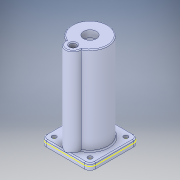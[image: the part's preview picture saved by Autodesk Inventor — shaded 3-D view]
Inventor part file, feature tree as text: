
AUTODESK INVENTOR PART (.ipt)
format: ipt  version: 2018 (Build 220112000, 112)  size: 350,208 bytes
history: native  units: in
note: dims shown in document units (in); Inventor stores cm internally (conversion verified against a paired STEP export)
features: extrude x16, sketch x13, projected_geometry x13, fillet x6, chamfer x1, revolve x1, other x1
ambient origin geometry x8: Origin, YZ Plane, XZ Plane, XY Plane, X Axis, Y Axis, Z Axis, Center Point
bodies: Solid1 (feature_tree)
feature tree (51):
  extrude  "Extrusion1"  TaperAngle=0.0deg  [1 undecoded]
  sketch  "Sketch2"  dims[d4=0.3937in d5=0.0in d6=1.0in d7=0.0in]
  extrude  "Extrusion2"  Depth=1.0in TaperAngle=0.0deg
  extrude  "Extrusion3"  Depth=0.9252in
  sketch  "Sketch3"  dims[d8=2.0in d9=0.0in d10=0.9252in]
  extrude  "Extrusion4"  Depth=2.0in TaperAngle=0.0deg
  extrude  "Extrusion5"  Depth=1.0in
  extrude  "Extrusion6"  Depth=0.3937in TaperAngle=0.0deg
  fillet  "Fillet2"  Radius=0.3937in
  fillet  "Fillet3"  Radius=0.45in
  sketch  "Sketch5"  dims[d14=0.5in d15=1.0in]
  extrude  "Extrusion7"  Depth=0.125in
  extrude  "Extrusion9"  TaperAngle=0.0deg  [1 undecoded]
  extrude  "Extrusion10"  Depth=0.9375in
  fillet  "Fillet4"  Radius=0.5in
  extrude  "Extrusion11"  Depth=0.0625in TaperAngle=45.0deg
  sketch  "Sketch9"  dims[d27=0.0in d28=0.0in d29=0.0in d30=0.0in]
  extrude  "Extrusion12"  Depth=0.25in TaperAngle=0.0deg
  extrude  "Extrusion13"  Depth=0.25in TaperAngle=0.0deg
  extrude  "Extrusion14"  Depth=1.374in
  fillet  "Fillet5"  [1 undecoded]
  chamfer  "Chamfer2"  [1 undecoded]
  fillet  "Fillet6"  [1 undecoded]
  sketch  "Sketch13"  dims[d46=0.25in d47=0.0in d48=0.25in d49=0.0in]
  extrude  "Extrusion15"  [1 undecoded]
  extrude  "Extrusion16"  [1 undecoded]
  extrude  "Extrusion17"  [1 undecoded]
  revolve  "Revolution1"  [1 undecoded]
  fillet  "Fillet1"  [1 undecoded]
  sketch  "Sketch1"  dims[d0=0.0in d1=0.0in d2=0.0in d3=0.0in]
  projected_geometry  "Projected Loop1"
  projected_geometry  "Projected Loop2"
  projected_geometry  "Projected Loop3"
  sketch  "Sketch4"  dims[d11=0.45in d12=2.0in d13=0.0in]
  projected_geometry  "Projected Loop4"
  sketch  "Sketch7"  dims[d16=1.0976in d17=0.3937in d18=0.0in d21=0.3937in d22=0.0in d23=0.45in]
  projected_geometry  "Projected Loop6"
  sketch  "Sketch8"  dims[d24=0.9843in d25=0.0in d26=0.125in]
  projected_geometry  "Projected Loop7"
  projected_geometry  "Projected Loop8"
  sketch  "Sketch10"  dims[d31=0.5in d32=0.0in d33=0.9375in d34=0.5in d35=0.0in]
  projected_geometry  "Projected Loop9"
  sketch  "Sketch11"  dims[d39=1.0in d40=0.0625in d41=0.0787in d42=45.0deg]
  projected_geometry  "Projected Loop10"
  sketch  "Sketch12"  dims[d43=0.0625in d44=0.25in d45=0.0in]
  projected_geometry  "Projected Loop11"
  sketch  "Sketch14"  dims[d51=0.125in d52=1.374in d53=90.0deg]
  projected_geometry  "Projected Loop12"
  projected_geometry  "Projected Loop13"
  projected_geometry  "Projected Loop14"
  other  "Ø8.0mm Dowel Hole1"
note: 10 required parameter values undecoded (feature->parameter linkage not recoverable at this tier; creation-order binding heuristic only, values carry confidence <= 0.55)
